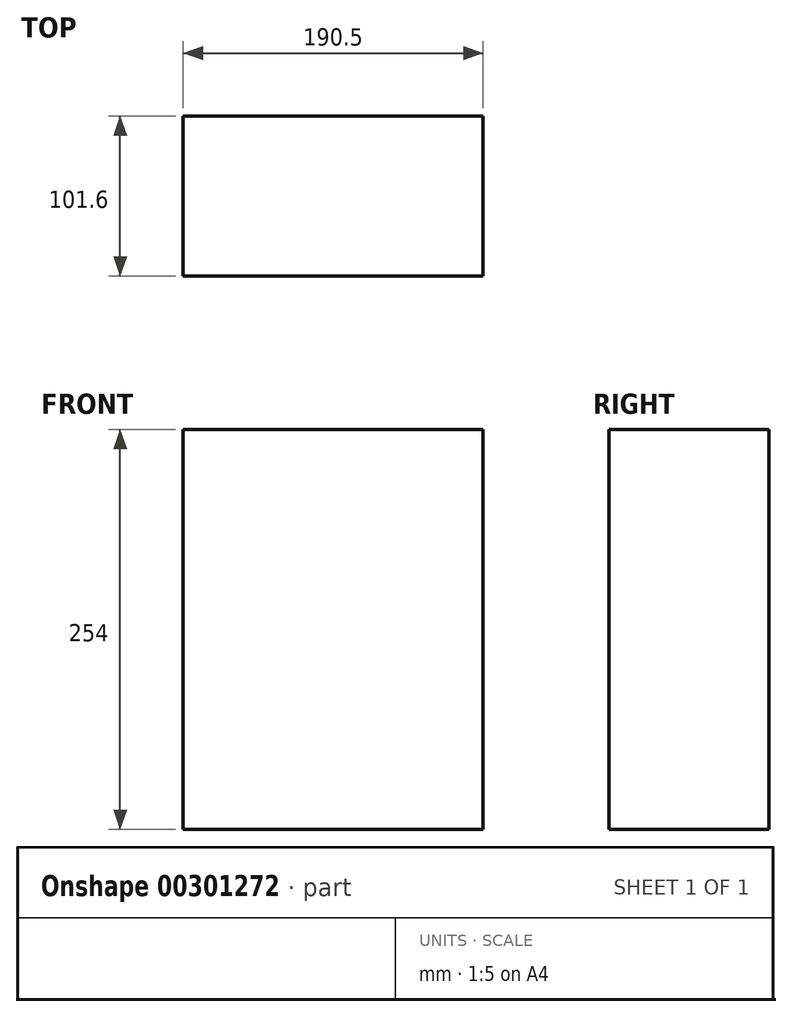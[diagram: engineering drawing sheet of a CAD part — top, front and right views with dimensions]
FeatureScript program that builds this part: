
annotation { "Feature Type Name" : "Feature", "Feature Type Description" : "" }
export const myFeature = defineFeature(function(context is Context, id is Id, definition is map)
    precondition{}
    {
        {
            var Q0;
            Q0=qCreatedBy(makeId("Front.planeOp"),FACE);
            var sketch = newSketch(context, id + "F0", { "sketchPlane" : qUnion([Q0])});
            skLineSegment(sketch, "E0.bottom", {"start": v(0, 0) * mm, "end": v(190.5, 0) * mm});
            skLineSegment(sketch, "E0.top", {"start": v(0, 254) * mm, "end": v(190.5, 254) * mm});
            skLineSegment(sketch, "E0.left", {"start": v(0, 0) * mm, "end": v(0, 254) * mm});
            skLineSegment(sketch, "E0.right", {"start": v(190.5, 0) * mm, "end": v(190.5, 254) * mm});
            skSolve(sketch);
        }
        {
            var Q0;
            Q0 = qSketchRegion(id + "F0", true);
            extrude(context, id + "F1", {"entities" : qUnion([Q0]), "depth" : 101.6 * mm});
        }
    });
